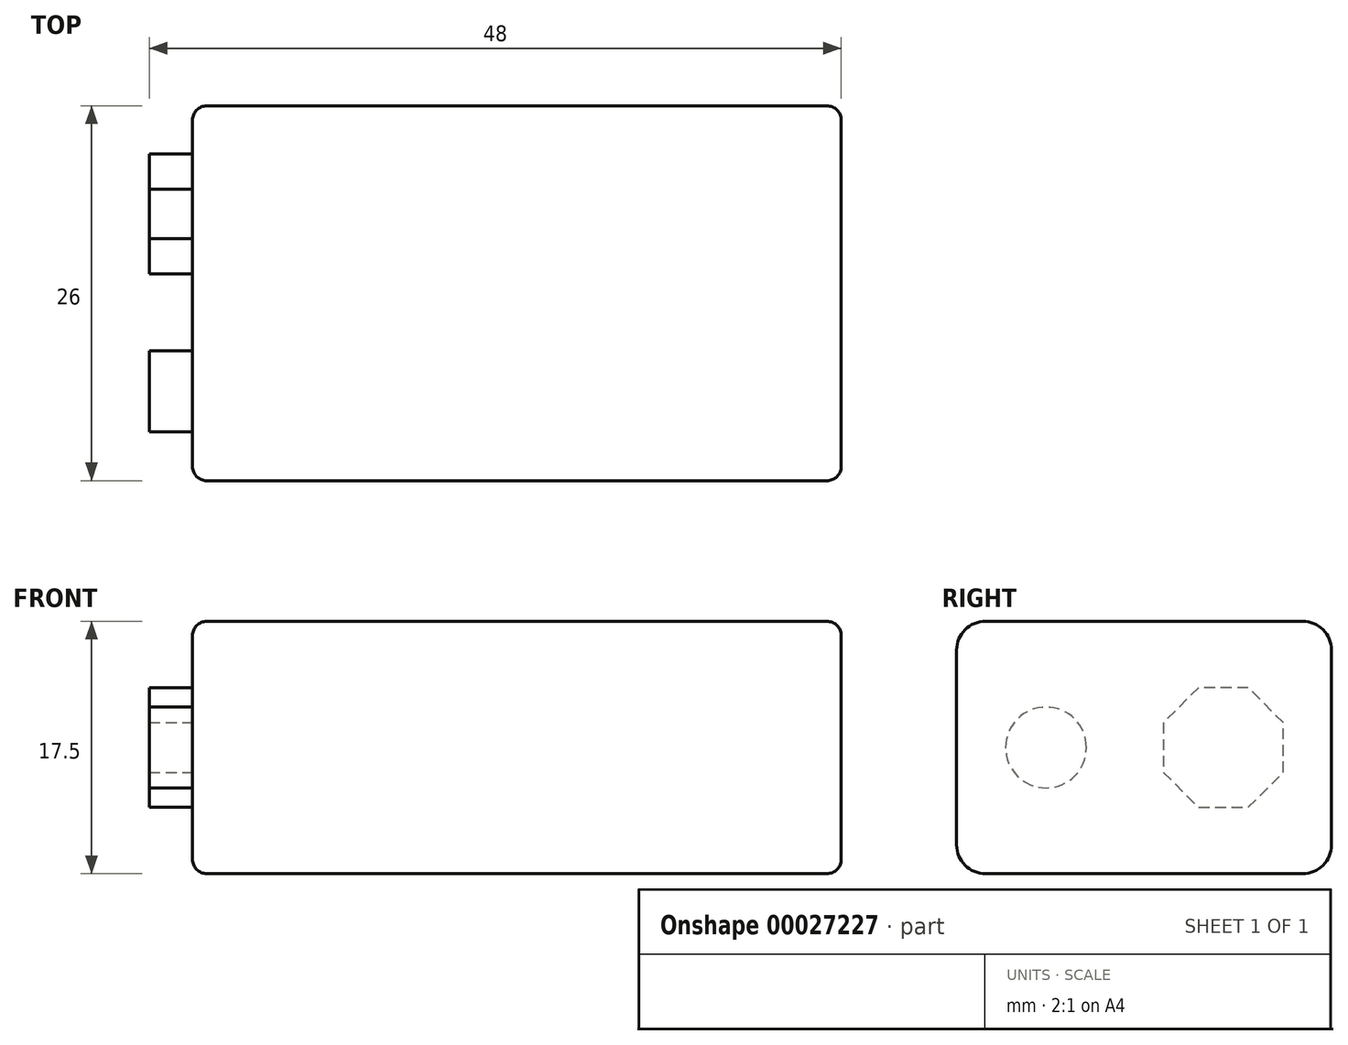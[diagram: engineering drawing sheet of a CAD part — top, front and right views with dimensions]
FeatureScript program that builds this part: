
annotation { "Feature Type Name" : "Feature", "Feature Type Description" : "" }
export const myFeature = defineFeature(function(context is Context, id is Id, definition is map)
    precondition{}
    {
        {
            var Q0;
            Q0=qCreatedBy(makeId("Top.planeOp"),FACE);
            var sketch = newSketch(context, id + "F0", { "sketchPlane" : qUnion([Q0])});
            skLineSegment(sketch, "E0.rect.bottom", {"start": v(22.5, 13) * mm, "end": v(-22.5, 13) * mm});
            skLineSegment(sketch, "E0.rect.top", {"start": v(22.5, -13) * mm, "end": v(-22.5, -13) * mm});
            skLineSegment(sketch, "E0.rect.left", {"start": v(22.5, 13) * mm, "end": v(22.5, -13) * mm});
            skLineSegment(sketch, "E0.rect.right", {"start": v(-22.5, 13) * mm, "end": v(-22.5, -13) * mm});
            skPoint(sketch, "E0.rect.middle", {"position": v(0, 0) * mm});
            skSolve(sketch);
        }
        {
            var Q0;
            Q0 = qSketchRegion(id + "F0", true);
            extrude(context, id + "F1", {"entities" : qUnion([Q0]), "depth" : 17.5 * mm});
        }
        {
            var Q0;
            Q0=makeQuery(id+"F1.opExtrude","SWEPT_FACE",FACE,{"disambiguationData":[OSD([sQuery(id+"F0.wireOp",EDGE,"E0.rect.right")])]});
            var sketch = newSketch(context, id + "F2", { "sketchPlane" : qUnion([Q0])});
            skCircle(sketch, "E1", {"center": v(6.8, 8.75) * mm, "radius": 2.8 * mm});
            skLineSegment(sketch, "E2", {"start": v(-13, 8.75) * mm, "end": v(13, 8.75) * mm, "construction": true});
            skCircle(sketch, "E3.cCircle", {"center": v(-5.5, 8.75) * mm, "radius": 4.5 * mm, "construction": true});
            skLineSegment(sketch, "E3.0", {"start": v(-3.78, 4.6) * mm, "end": v(-7.22, 4.6) * mm});
            skLineSegment(sketch, "E3.1", {"start": v(-7.22, 4.6) * mm, "end": v(-9.66, 7.03) * mm});
            skLineSegment(sketch, "E3.2", {"start": v(-9.66, 7.03) * mm, "end": v(-9.66, 10.47) * mm});
            skLineSegment(sketch, "E3.3", {"start": v(-9.66, 10.47) * mm, "end": v(-7.22, 12.9) * mm});
            skLineSegment(sketch, "E3.4", {"start": v(-7.22, 12.9) * mm, "end": v(-3.78, 12.9) * mm});
            skLineSegment(sketch, "E3.5", {"start": v(-3.78, 12.9) * mm, "end": v(-1.34, 10.47) * mm});
            skLineSegment(sketch, "E3.6", {"start": v(-1.34, 10.47) * mm, "end": v(-1.34, 7.03) * mm});
            skLineSegment(sketch, "E3.7", {"start": v(-1.34, 7.03) * mm, "end": v(-3.78, 4.6) * mm});
            skSolve(sketch);
        }
        {
            var Q0;
            Q0 = qSketchRegion(id + "F2", true);
            extrude(context, id + "F3", {"entities" : qUnion([Q0]), "operationType" : NewBodyOperationType.ADD, "depth" : 3 * mm});
        }
        {
            var Q0;
            Q0=makeQuery(id+"F1.opExtrude","CAP_EDGE",EDGE,{"disambiguationData":[OSD([sQuery(id+"F0.wireOp",EDGE,"E0.rect.bottom")])],"isStart":false});
            var Q1;
            Q1=makeQuery(id+"F1.opExtrude","CAP_EDGE",EDGE,{"disambiguationData":[OSD([sQuery(id+"F0.wireOp",EDGE,"E0.rect.bottom")])],"isStart":true});
            var Q2;
            Q2=makeQuery(id+"F1.opExtrude","CAP_EDGE",EDGE,{"disambiguationData":[OSD([sQuery(id+"F0.wireOp",EDGE,"E0.rect.top")])],"isStart":false});
            var Q3;
            Q3=makeQuery(id+"F1.opExtrude","CAP_EDGE",EDGE,{"disambiguationData":[OSD([sQuery(id+"F0.wireOp",EDGE,"E0.rect.top")])],"isStart":true});
            fillet(context, id + "F4", {"entities" : qUnion([Q0, Q1, Q2, Q3]), "radius" : 2 * mm, "tangentPropagation" : true, "allowEdgeOverflow" : false});
        }
        {
            var Q0;
            Q0=makeQuery(id+"F1.opExtrude","CAP_EDGE",EDGE,{"disambiguationData":[OSD([sQuery(id+"F0.wireOp",EDGE,"E0.rect.right")])],"isStart":false});
            var Q1;
            Q1=makeQuery(id+"F1.opExtrude","CAP_EDGE",EDGE,{"disambiguationData":[OSD([sQuery(id+"F0.wireOp",EDGE,"E0.rect.left")])],"isStart":false});
            fillet(context, id + "F5", {"entities" : qUnion([Q0, Q1]), "radius" : 1 * mm, "tangentPropagation" : true, "allowEdgeOverflow" : false});
        }
    });
